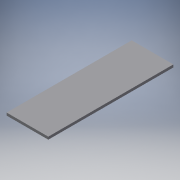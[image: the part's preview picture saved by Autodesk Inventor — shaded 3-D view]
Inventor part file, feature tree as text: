
AUTODESK INVENTOR PART (.ipt)
format: ipt  version: 2017 (Build 210142000, 142)  size: 89,600 bytes
history: native  units: in
note: dims shown in document units (in); Inventor stores cm internally (conversion verified against a paired STEP export)
features: extrude x1, sketch x1
ambient origin geometry x8: Origin, YZ Plane, XZ Plane, XY Plane, X Axis, Y Axis, Z Axis, Center Point
bodies: Solid1 (feature_tree)
feature tree (2):
  extrude  "Extrusion1"  Depth=4.0in
  sketch  "Sketch1"  dims[d0=12.0in d1=4.0in d2=0.25in d3=0.0in]
